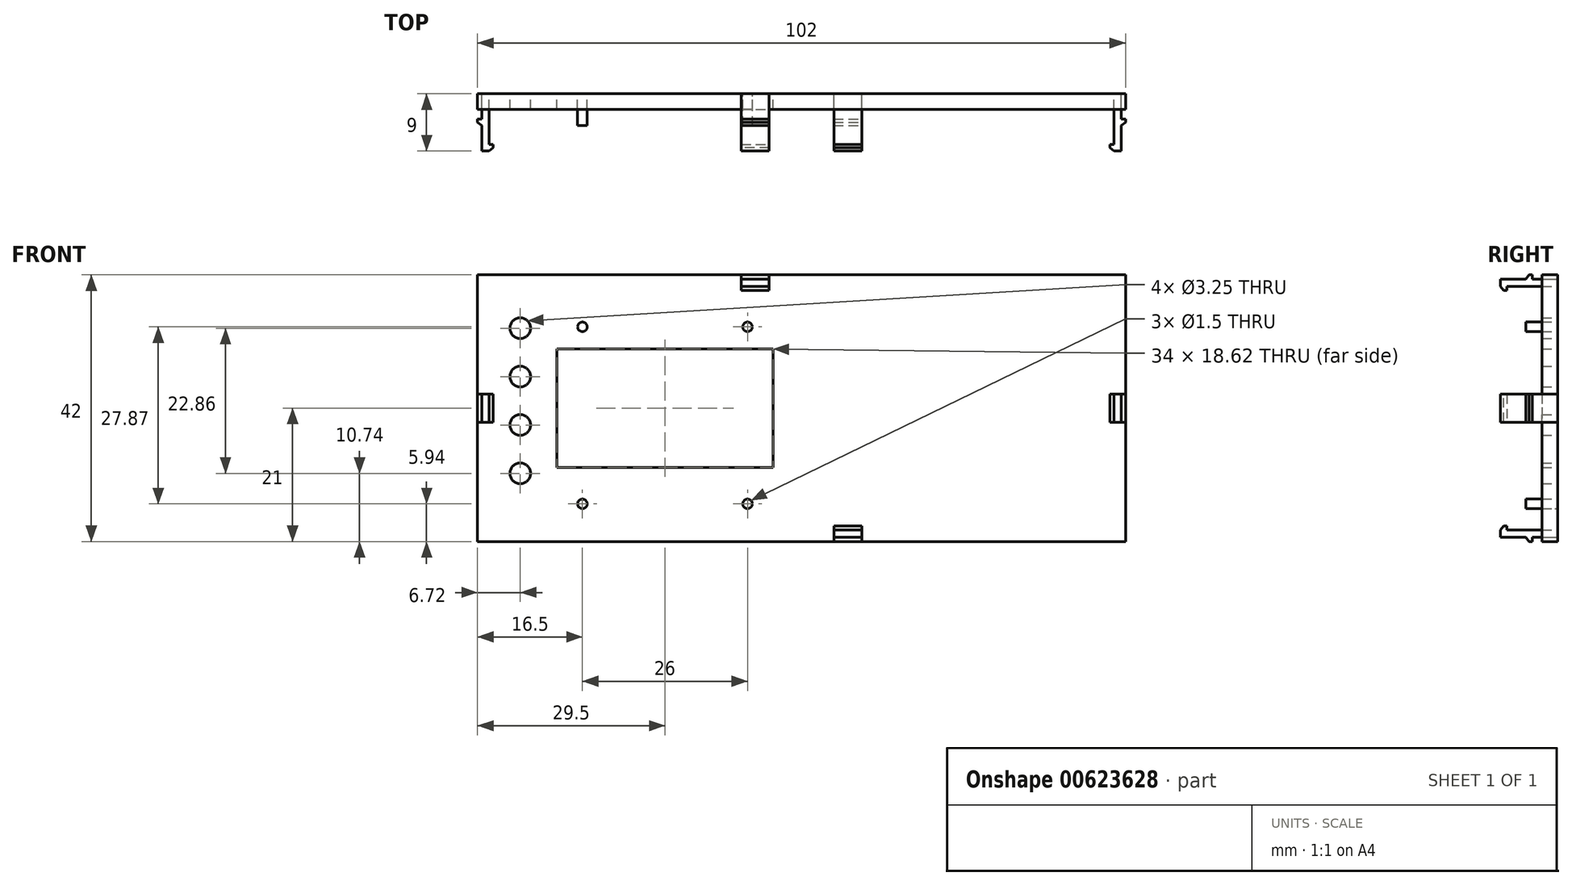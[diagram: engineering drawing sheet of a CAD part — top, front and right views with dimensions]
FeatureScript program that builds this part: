
annotation { "Feature Type Name" : "Feature", "Feature Type Description" : "" }
export const myFeature = defineFeature(function(context is Context, id is Id, definition is map)
    precondition{}
    {
        {
            var Q0;
            Q0=qCreatedBy(makeId("Front.planeOp"),FACE);
            var sketch = newSketch(context, id + "F0", { "sketchPlane" : qUnion([Q0])});
            skLineSegment(sketch, "E0.bottom", {"start": v(-51, 21) * mm, "end": v(-9.5, 21) * mm});
            skLineSegment(sketch, "E0.top", {"start": v(-51, -21) * mm, "end": v(5.1, -21) * mm});
            skLineSegment(sketch, "E0.left", {"start": v(-51, 21) * mm, "end": v(-51, 2.2) * mm});
            skLineSegment(sketch, "E0.right", {"start": v(51, 21) * mm, "end": v(51, 2.2) * mm});
            skPoint(sketch, "E0.middle", {"position": v(0, 0) * mm});
            skLineSegment(sketch, "E1", {"start": v(-50.35, 2.2) * mm, "end": v(-50.35, -2.2) * mm});
            skLineSegment(sketch, "E2", {"start": v(-50.35, -2.2) * mm, "end": v(-51, -2.2) * mm});
            skLineSegment(sketch, "E3", {"start": v(-50.35, 2.2) * mm, "end": v(-51, 2.2) * mm});
            skLineSegment(sketch, "E4.trimOffspring", {"start": v(-51, -2.2) * mm, "end": v(-51, -21) * mm});
            skLineSegment(sketch, "E5", {"start": v(-9.5, 21) * mm, "end": v(-9.5, 20.35) * mm});
            skLineSegment(sketch, "E6", {"start": v(-9.5, 20.35) * mm, "end": v(-5.1, 20.35) * mm});
            skLineSegment(sketch, "E7", {"start": v(-5.1, 20.35) * mm, "end": v(-5.1, 21) * mm});
            skLineSegment(sketch, "E8.trimOffspring", {"start": v(-5.1, 21) * mm, "end": v(51, 21) * mm});
            skLineSegment(sketch, "E9", {"start": v(5.1, -21) * mm, "end": v(5.1, -20.35) * mm});
            skLineSegment(sketch, "E10", {"start": v(5.1, -20.35) * mm, "end": v(9.5, -20.35) * mm});
            skLineSegment(sketch, "E11", {"start": v(9.5, -20.35) * mm, "end": v(9.5, -21) * mm});
            skLineSegment(sketch, "E12", {"start": v(51, 2.2) * mm, "end": v(50.35, 2.2) * mm});
            skLineSegment(sketch, "E13", {"start": v(50.35, 2.2) * mm, "end": v(50.35, -2.2) * mm});
            skLineSegment(sketch, "E14", {"start": v(50.35, -2.2) * mm, "end": v(51, -2.2) * mm});
            skLineSegment(sketch, "E15.trimOffspring", {"start": v(9.5, -21) * mm, "end": v(51, -21) * mm});
            skLineSegment(sketch, "E16.trimOffspring", {"start": v(51, -2.2) * mm, "end": v(51, -21) * mm});
            skLineSegment(sketch, "E17", {"start": v(-9.5, 20.35) * mm, "end": v(-9.5, 19.2) * mm});
            skLineSegment(sketch, "E18", {"start": v(-9.5, 19.2) * mm, "end": v(-5.1, 19.2) * mm});
            skLineSegment(sketch, "E19", {"start": v(-5.1, 19.2) * mm, "end": v(-5.1, 20.35) * mm});
            skLineSegment(sketch, "E20", {"start": v(-50.35, 2.2) * mm, "end": v(-49.2, 2.2) * mm});
            skLineSegment(sketch, "E21", {"start": v(-49.2, 2.2) * mm, "end": v(-49.2, -2.2) * mm});
            skLineSegment(sketch, "E22", {"start": v(-49.2, -2.2) * mm, "end": v(-50.35, -2.2) * mm});
            skLineSegment(sketch, "E23", {"start": v(5.1, -20.35) * mm, "end": v(5.1, -19.2) * mm});
            skLineSegment(sketch, "E24", {"start": v(5.1, -19.2) * mm, "end": v(9.5, -19.2) * mm});
            skLineSegment(sketch, "E25", {"start": v(9.5, -19.2) * mm, "end": v(9.5, -20.35) * mm});
            skLineSegment(sketch, "E26", {"start": v(50.35, 2.2) * mm, "end": v(49.2, 2.2) * mm});
            skLineSegment(sketch, "E27", {"start": v(49.2, 2.2) * mm, "end": v(49.2, -2.2) * mm});
            skLineSegment(sketch, "E28", {"start": v(49.2, -2.2) * mm, "end": v(50.35, -2.2) * mm});
            skLineSegment(sketch, "E29.bottom", {"start": v(-38.5, 9.3) * mm, "end": v(-4.5, 9.3) * mm});
            skLineSegment(sketch, "E29.top", {"start": v(-38.5, -9.31) * mm, "end": v(-4.5, -9.31) * mm});
            skLineSegment(sketch, "E29.left", {"start": v(-38.5, 9.3) * mm, "end": v(-38.5, -9.31) * mm});
            skLineSegment(sketch, "E29.right", {"start": v(-4.5, 9.3) * mm, "end": v(-4.5, -9.31) * mm});
            skCircle(sketch, "E30", {"center": v(-44.28, 12.6) * mm, "radius": 1.63 * mm});
            skCircle(sketch, "E31", {"center": v(-44.28, -10.26) * mm, "radius": 1.63 * mm});
            skCircle(sketch, "E32", {"center": v(-44.28, 4.98) * mm, "radius": 1.63 * mm});
            skCircle(sketch, "E33", {"center": v(-44.28, -2.64) * mm, "radius": 1.63 * mm});
            skCircle(sketch, "E34", {"center": v(-34.5, 12.8) * mm, "radius": 0.75 * mm});
            skCircle(sketch, "E35", {"center": v(-8.5, 12.8) * mm, "radius": 0.75 * mm});
            skCircle(sketch, "E36", {"center": v(-34.5, -15.06) * mm, "radius": 0.75 * mm});
            skCircle(sketch, "E37", {"center": v(-8.5, -15.06) * mm, "radius": 0.75 * mm});
            skSolve(sketch);
        }
        {
            var Q0;
            Q0=makeQuery(id+"F0.imprint","IMPRINT",FACE,{"disambiguationData":[TD([[makeQuery(id+"F0.imprint","IMPRINT",EDGE,{"derivedFrom":sQuery(id+"F0.wireOp",EDGE,"E0.bottom")}),-1.0]])]});
            extrude(context, id + "F1", {"entities" : qUnion([Q0]), "depth" : 2.45 * mm, "offsetDistance" : 25 * mm});
        }
        {
            var Q0;
            Q0=makeQuery(id+"F0.imprint","IMPRINT",FACE,{"disambiguationData":[TD([[makeQuery(id+"F0.imprint","IMPRINT",EDGE,{"derivedFrom":sQuery(id+"F0.wireOp",EDGE,"E6")}),-1.0]])]});
            var Q1;
            Q1=makeQuery(id+"F0.imprint","IMPRINT",FACE,{"disambiguationData":[TD([[makeQuery(id+"F0.imprint","IMPRINT",EDGE,{"derivedFrom":sQuery(id+"F0.wireOp",EDGE,"E1")}),1.0]])]});
            var Q2;
            Q2=makeQuery(id+"F0.imprint","IMPRINT",FACE,{"disambiguationData":[TD([[makeQuery(id+"F0.imprint","IMPRINT",EDGE,{"derivedFrom":sQuery(id+"F0.wireOp",EDGE,"E13")}),-1.0]])]});
            var Q3;
            Q3=makeQuery(id+"F0.imprint","IMPRINT",FACE,{"disambiguationData":[TD([[makeQuery(id+"F0.imprint","IMPRINT",EDGE,{"derivedFrom":sQuery(id+"F0.wireOp",EDGE,"E10")}),1.0]])]});
            extrude(context, id + "F2", {"entities" : qUnion([Q0, Q1, Q2, Q3]), "depth" : 8 * mm, "offsetDistance" : 25 * mm});
        }
        {
            var Q0;
            Q0=makeQuery(id+"F0.imprint","IMPRINT",FACE,{"disambiguationData":[TD([[makeQuery(id+"F0.imprint","IMPRINT",EDGE,{"derivedFrom":sQuery(id+"F0.wireOp",EDGE,"E34")}),1.0]])]});
            extrude(context, id + "F3", {"entities" : qUnion([Q0]), "operationType" : NewBodyOperationType.ADD, "depth" : 5 * mm, "offsetDistance" : 25 * mm});
        }
        {
            var Q0;
            Q0=makeQuery(id+"F0.imprint","IMPRINT",FACE,{"disambiguationData":[TD([[makeQuery(id+"F0.imprint","IMPRINT",EDGE,{"derivedFrom":sQuery(id+"F0.wireOp",EDGE,"E35")}),1.0]])]});
            var Q1;
            Q1=sQuery(id+"F0.wireOp",EDGE,"E35");
            extrude(context, id + "F4", {"entities" : qUnion([Q0]), "surfaceEntities" : qUnion([Q1]), "depth" : 5 * mm, "offsetDistance" : 25 * mm});
        }
        {
            var Q0;
            Q0=makeQuery(id+"F0.imprint","IMPRINT",FACE,{"disambiguationData":[TD([[makeQuery(id+"F0.imprint","IMPRINT",EDGE,{"derivedFrom":sQuery(id+"F0.wireOp",EDGE,"E36")}),1.0]])]});
            var Q1;
            Q1=makeQuery(id+"F0.imprint","IMPRINT",FACE,{"disambiguationData":[TD([[makeQuery(id+"F0.imprint","IMPRINT",EDGE,{"derivedFrom":sQuery(id+"F0.wireOp",EDGE,"E37")}),1.0]])]});
            var Q2;
            Q2=sQuery(id+"F0.wireOp",EDGE,"E36");
            var Q3;
            Q3=sQuery(id+"F0.wireOp",EDGE,"E37");
            extrude(context, id + "F5", {"entities" : qUnion([Q0, Q1]), "surfaceEntities" : qUnion([Q2, Q3]), "depth" : 5 * mm, "offsetDistance" : 25 * mm});
        }
        {
            var Q0;
            Q0=makeQuery(id+"F2.opExtrude","SWEPT_FACE",FACE,{"disambiguationData":[OSD([sQuery(id+"F0.wireOp",EDGE,"E17")])]});
            var sketch = newSketch(context, id + "F6", { "sketchPlane" : qUnion([Q0])});
            skLineSegment(sketch, "E38", {"start": v(4, 20.35) * mm, "end": v(4, 21) * mm});
            skLineSegment(sketch, "E39", {"start": v(4, 21) * mm, "end": v(4.5, 21) * mm});
            skLineSegment(sketch, "E40", {"start": v(4.5, 21) * mm, "end": v(5, 20.35) * mm});
            skLineSegment(sketch, "E41", {"start": v(8, 20.35) * mm, "end": v(9, 20.35) * mm});
            skLineSegment(sketch, "E42", {"start": v(9, 20.35) * mm, "end": v(9, 19.2) * mm});
            skLineSegment(sketch, "E43", {"start": v(9, 19.2) * mm, "end": v(8.5, 18.55) * mm});
            skLineSegment(sketch, "E44", {"start": v(8.5, 18.55) * mm, "end": v(8, 18.55) * mm});
            skLineSegment(sketch, "E45", {"start": v(8, 18.55) * mm, "end": v(8, 19.2) * mm});
            skSolve(sketch);
        }
        {
            var Q0;
            Q0=makeQuery(id+"F2.opExtrude","SWEPT_FACE",FACE,{"disambiguationData":[OSD([sQuery(id+"F0.wireOp",EDGE,"E22")])]});
            var sketch = newSketch(context, id + "F7", { "sketchPlane" : qUnion([Q0])});
            skLineSegment(sketch, "E46", {"start": v(-50.35, 4) * mm, "end": v(-51, 4) * mm});
            skLineSegment(sketch, "E47", {"start": v(-51, 4) * mm, "end": v(-51, 4.5) * mm});
            skLineSegment(sketch, "E48", {"start": v(-51, 4.5) * mm, "end": v(-50.35, 5) * mm});
            skLineSegment(sketch, "E49", {"start": v(-50.35, 8) * mm, "end": v(-50.35, 9) * mm});
            skLineSegment(sketch, "E50", {"start": v(-50.35, 9) * mm, "end": v(-49.2, 9) * mm});
            skLineSegment(sketch, "E51", {"start": v(-49.2, 9) * mm, "end": v(-48.55, 8.5) * mm});
            skLineSegment(sketch, "E52", {"start": v(-48.55, 8.5) * mm, "end": v(-48.55, 8) * mm});
            skLineSegment(sketch, "E53", {"start": v(-48.55, 8) * mm, "end": v(-49.2, 8) * mm});
            skSolve(sketch);
        }
        {
            var Q0;
            Q0=makeQuery(id+"F2.opExtrude","SWEPT_FACE",FACE,{"disambiguationData":[OSD([sQuery(id+"F0.wireOp",EDGE,"E25")])]});
            var sketch = newSketch(context, id + "F8", { "sketchPlane" : qUnion([Q0])});
            skLineSegment(sketch, "E54", {"start": v(-4, -20.35) * mm, "end": v(-4, -21) * mm});
            skLineSegment(sketch, "E55", {"start": v(-4, -21) * mm, "end": v(-4.5, -21) * mm});
            skLineSegment(sketch, "E56", {"start": v(-4.5, -21) * mm, "end": v(-5, -20.35) * mm});
            skLineSegment(sketch, "E57", {"start": v(-8, -20.35) * mm, "end": v(-9, -20.35) * mm});
            skLineSegment(sketch, "E58", {"start": v(-9, -20.35) * mm, "end": v(-9, -19.2) * mm});
            skLineSegment(sketch, "E59", {"start": v(-9, -19.2) * mm, "end": v(-8.5, -18.55) * mm});
            skLineSegment(sketch, "E60", {"start": v(-8.5, -18.55) * mm, "end": v(-8, -18.55) * mm});
            skLineSegment(sketch, "E61", {"start": v(-8, -18.55) * mm, "end": v(-8, -19.2) * mm});
            skSolve(sketch);
        }
        {
            var Q0;
            Q0=makeQuery(id+"F2.opExtrude","SWEPT_FACE",FACE,{"disambiguationData":[OSD([sQuery(id+"F0.wireOp",EDGE,"E26")])]});
            var sketch = newSketch(context, id + "F9", { "sketchPlane" : qUnion([Q0])});
            skLineSegment(sketch, "E62", {"start": v(50.35, -4) * mm, "end": v(51, -4) * mm});
            skLineSegment(sketch, "E63", {"start": v(51, -4) * mm, "end": v(51, -4.5) * mm});
            skLineSegment(sketch, "E64", {"start": v(51, -4.5) * mm, "end": v(50.35, -5) * mm});
            skLineSegment(sketch, "E65", {"start": v(50.35, -8) * mm, "end": v(50.35, -9) * mm});
            skLineSegment(sketch, "E66", {"start": v(50.35, -9) * mm, "end": v(49.2, -9) * mm});
            skLineSegment(sketch, "E67", {"start": v(49.2, -9) * mm, "end": v(48.55, -8.5) * mm});
            skLineSegment(sketch, "E68", {"start": v(48.55, -8.5) * mm, "end": v(48.55, -8) * mm});
            skLineSegment(sketch, "E69", {"start": v(48.55, -8) * mm, "end": v(49.2, -8) * mm});
            skSolve(sketch);
        }
        {
            var Q0;
            Q0=makeQuery(id+"F9.imprint","IMPRINT",FACE,{"disambiguationData":[TD([[makeQuery(id+"F9.imprint","IMPRINT",EDGE,{"derivedFrom":sQuery(id+"F9.wireOp",EDGE,"E65")}),-1.0]])]});
            var Q1;
            {var subQ0=sQuery(id+"F9.wireOp",EDGE,"E62");Q1=makeQuery(id+"F9.imprint","IMPRINT",FACE,{"disambiguationData":[TD([[makeQuery(id+"F9.imprint","IMPRINT",EDGE,{"derivedFrom":subQ0}),-1.0]])]});}
            extrude(context, id + "F10", {"entities" : qUnion([Q0, Q1]), "operationType" : NewBodyOperationType.ADD, "oppositeDirection" : true, "depth" : 4.4 * mm, "offsetDistance" : 25 * mm});
        }
        {
            var Q0;
            Q0=makeQuery(id+"F8.imprint","IMPRINT",FACE,{"disambiguationData":[TD([[makeQuery(id+"F8.imprint","IMPRINT",EDGE,{"derivedFrom":sQuery(id+"F8.wireOp",EDGE,"E57")}),-1.0]])]});
            var Q1;
            {var subQ0=sQuery(id+"F8.wireOp",EDGE,"E54");Q1=makeQuery(id+"F8.imprint","IMPRINT",FACE,{"disambiguationData":[TD([[makeQuery(id+"F8.imprint","IMPRINT",EDGE,{"derivedFrom":subQ0}),-1.0]])]});}
            extrude(context, id + "F11", {"entities" : qUnion([Q0, Q1]), "operationType" : NewBodyOperationType.ADD, "oppositeDirection" : true, "depth" : 4.4 * mm, "offsetDistance" : 25 * mm});
        }
        {
            var Q0;
            Q0=makeQuery(id+"F7.imprint","IMPRINT",FACE,{"disambiguationData":[TD([[makeQuery(id+"F7.imprint","IMPRINT",EDGE,{"derivedFrom":sQuery(id+"F7.wireOp",EDGE,"E49")}),-1.0]])]});
            var Q1;
            {var subQ0=sQuery(id+"F7.wireOp",EDGE,"E46");Q1=makeQuery(id+"F7.imprint","IMPRINT",FACE,{"disambiguationData":[TD([[makeQuery(id+"F7.imprint","IMPRINT",EDGE,{"derivedFrom":subQ0}),-1.0]])]});}
            extrude(context, id + "F12", {"entities" : qUnion([Q0, Q1]), "operationType" : NewBodyOperationType.ADD, "oppositeDirection" : true, "depth" : 4.4 * mm, "offsetDistance" : 25 * mm});
        }
        {
            var Q0;
            Q0=makeQuery(id+"F6.imprint","IMPRINT",FACE,{"disambiguationData":[TD([[makeQuery(id+"F6.imprint","IMPRINT",EDGE,{"derivedFrom":sQuery(id+"F6.wireOp",EDGE,"E41")}),-1.0]])]});
            var Q1;
            {var subQ0=sQuery(id+"F6.wireOp",EDGE,"E38");Q1=makeQuery(id+"F6.imprint","IMPRINT",FACE,{"disambiguationData":[TD([[makeQuery(id+"F6.imprint","IMPRINT",EDGE,{"derivedFrom":subQ0}),-1.0]])]});}
            extrude(context, id + "F13", {"entities" : qUnion([Q0, Q1]), "operationType" : NewBodyOperationType.ADD, "oppositeDirection" : true, "depth" : 4.4 * mm, "offsetDistance" : 25 * mm});
        }
    });
